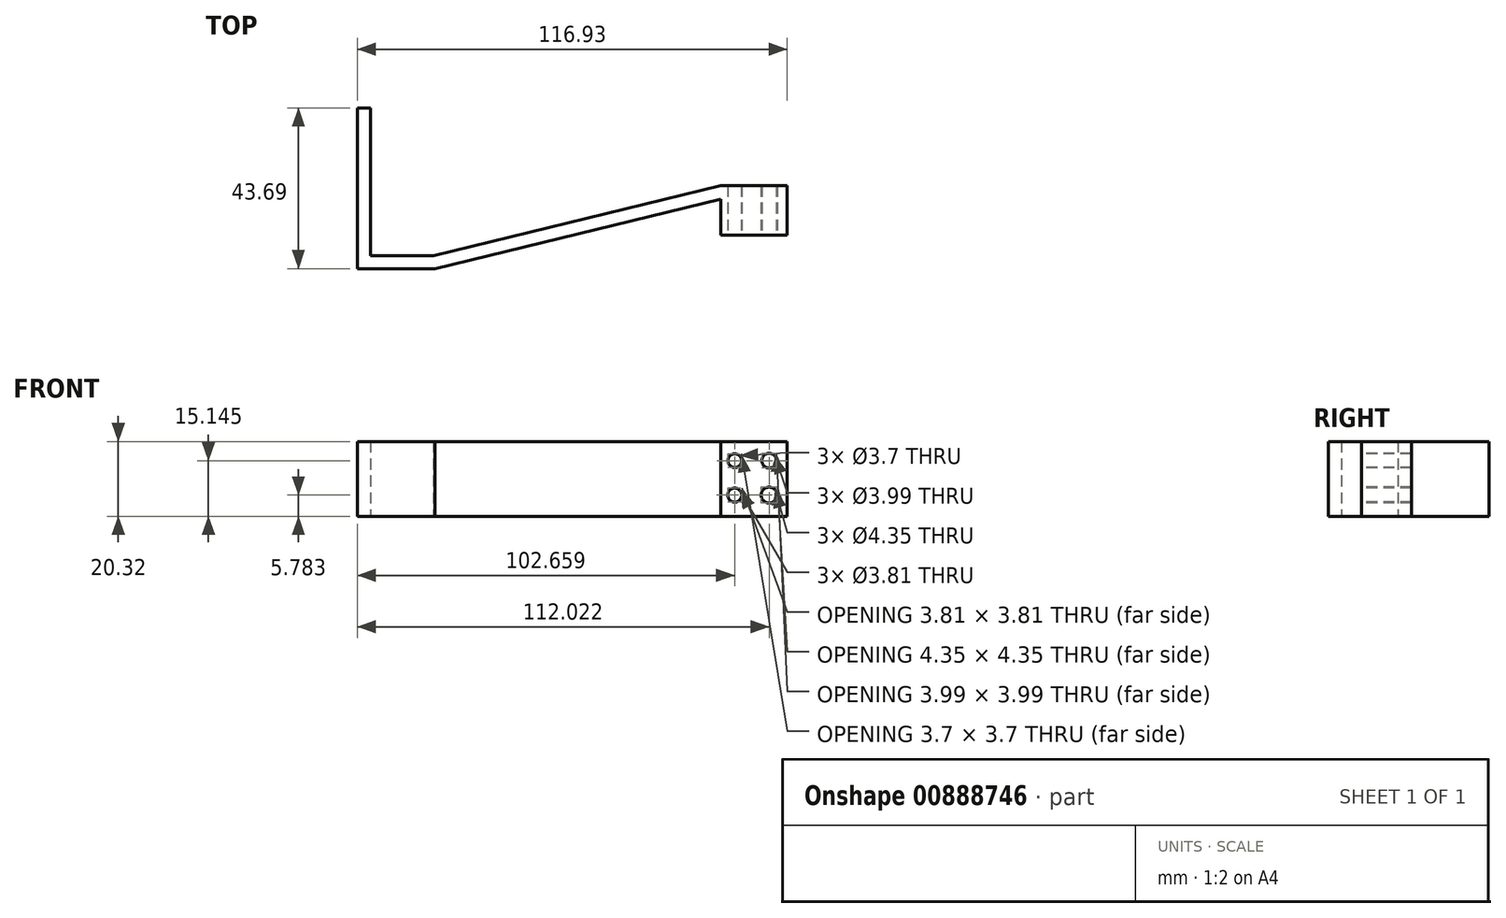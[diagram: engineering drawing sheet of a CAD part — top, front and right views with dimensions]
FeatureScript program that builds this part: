
annotation { "Feature Type Name" : "Feature", "Feature Type Description" : "" }
export const myFeature = defineFeature(function(context is Context, id is Id, definition is map)
    precondition{}
    {
        {
            var Q0;
            Q0=qCreatedBy(makeId("Top.planeOp"),FACE);
            var sketch = newSketch(context, id + "F0", { "sketchPlane" : qUnion([Q0])});
            skLineSegment(sketch, "E0", {"start": v(-88.4, 29.72) * mm, "end": v(-88.4, -10.42) * mm});
            skLineSegment(sketch, "E1", {"start": v(-88.4, -10.42) * mm, "end": v(-71.24, -10.42) * mm});
            skLineSegment(sketch, "E2", {"start": v(-71.24, -10.42) * mm, "end": v(6.89, 8.58) * mm});
            skLineSegment(sketch, "E3", {"start": v(6.89, 8.58) * mm, "end": v(24.97, 8.58) * mm});
            skLineSegment(sketch, "E4", {"start": v(24.97, 8.58) * mm, "end": v(24.97, -4.9) * mm});
            skLineSegment(sketch, "E5", {"start": v(24.97, -4.9) * mm, "end": v(6.89, -4.9) * mm});
            skLineSegment(sketch, "E6", {"start": v(6.89, -4.9) * mm, "end": v(6.89, 8.58) * mm});
            skLineSegment(sketch, "E7.0", {"start": v(-70.82, -13.97) * mm, "end": v(6.89, 4.92) * mm});
            skLineSegment(sketch, "E7.1", {"start": v(-91.96, -13.97) * mm, "end": v(-70.82, -13.97) * mm});
            skLineSegment(sketch, "E7.2", {"start": v(-91.96, 29.72) * mm, "end": v(-91.96, -13.97) * mm});
            skLineSegment(sketch, "E8", {"start": v(-91.96, 29.72) * mm, "end": v(-88.4, 29.72) * mm});
            skSolve(sketch);
        }
        {
            var Q0;
            {var subQ3=sQuery(id+"F0.wireOp",EDGE,"E3");Q0=makeQuery(id+"F0.imprint","IMPRINT",FACE,{"disambiguationData":[TD([[makeQuery(id+"F0.imprint","IMPRINT",EDGE,{"derivedFrom":subQ3}),-1.0]])]});}
            var Q1;
            Q1=makeQuery(id+"F0.imprint","IMPRINT",FACE,{"disambiguationData":[TD([[makeQuery(id+"F0.imprint","IMPRINT",EDGE,{"derivedFrom":sQuery(id+"F0.wireOp",EDGE,"E0")}),-1.0]])]});
            extrude(context, id + "F1", {"entities" : qUnion([Q0, Q1]), "depth" : 20.32 * mm, "offsetDistance" : 25.4 * mm});
        }
        {
            var Q0;
            Q0=makeQuery(id+"F1.opExtrude","SWEPT_FACE",FACE,{"disambiguationData":[OSD([sQuery(id+"F0.wireOp",EDGE,"E5")])]});
            var sketch = newSketch(context, id + "F2", { "sketchPlane" : qUnion([Q0])});
            skCircle(sketch, "E9", {"center": v(10.7, 15.15) * mm, "radius": 1.85 * mm});
            skCircle(sketch, "E10", {"center": v(20.06, 15.15) * mm, "radius": 2 * mm});
            skCircle(sketch, "E11", {"center": v(10.7, 5.78) * mm, "radius": 1.9 * mm});
            skCircle(sketch, "E12", {"center": v(20.06, 5.78) * mm, "radius": 2.18 * mm});
            skSolve(sketch);
        }
        {
            var Q0;
            Q0=makeQuery(id+"F2.imprint","IMPRINT",FACE,{"disambiguationData":[TD([[makeQuery(id+"F2.imprint","IMPRINT",EDGE,{"derivedFrom":sQuery(id+"F2.wireOp",EDGE,"E9")}),1.0]])]});
            var Q1;
            Q1=makeQuery(id+"F2.imprint","IMPRINT",FACE,{"disambiguationData":[TD([[makeQuery(id+"F2.imprint","IMPRINT",EDGE,{"derivedFrom":sQuery(id+"F2.wireOp",EDGE,"E10")}),1.0]])]});
            var Q2;
            Q2=makeQuery(id+"F2.imprint","IMPRINT",FACE,{"disambiguationData":[TD([[makeQuery(id+"F2.imprint","IMPRINT",EDGE,{"derivedFrom":sQuery(id+"F2.wireOp",EDGE,"E12")}),1.0]])]});
            var Q3;
            Q3=makeQuery(id+"F2.imprint","IMPRINT",FACE,{"disambiguationData":[TD([[makeQuery(id+"F2.imprint","IMPRINT",EDGE,{"derivedFrom":sQuery(id+"F2.wireOp",EDGE,"E11")}),1.0]])]});
            extrude(context, id + "F3", {"entities" : qUnion([Q0, Q1, Q2, Q3]), "operationType" : NewBodyOperationType.REMOVE, "endBound" : BoundingType.THROUGH_ALL, "oppositeDirection" : true, "depth" : 25.4 * mm, "offsetDistance" : 25.4 * mm});
        }
    });
